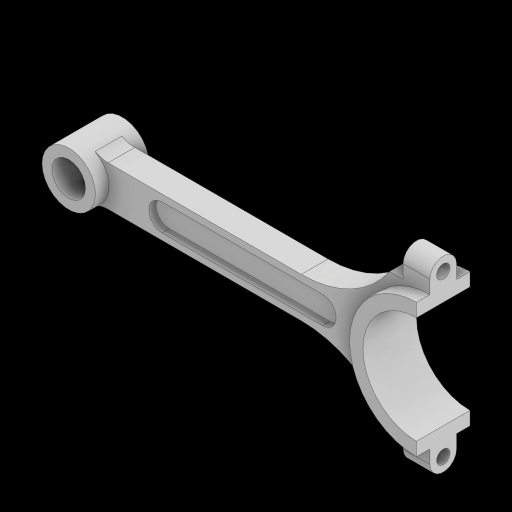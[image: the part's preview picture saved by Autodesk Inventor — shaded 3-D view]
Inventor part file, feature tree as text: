
AUTODESK INVENTOR PART (.ipt)
format: ipt  version: 2024 (Build 280153000, 153)  size: 208,384 bytes
history: native  units: in
note: dims shown in document units (in); Inventor stores cm internally (conversion verified against a paired STEP export)
features: sketch x3, extrude x3, fillet x2, mirror x2, hole x1
ambient origin geometry x8: Origin, YZ Plane, XZ Plane, XY Plane, X Axis, Y Axis, Z Axis, Center Point
bodies: Solid1 (feature_tree)
feature tree (11):
  sketch  "Sketch1"  dims[d0=2.0in d1=1.0in]
  extrude  "CENTER WEB"  Depth=1.0in
  extrude  "END RINGS"  Depth=0.625in
  fillet  "Fillet1"  Radius=2.5in
  fillet  "Fillet2"  Radius=0.75in
  hole  "Hole1"  [1 undecoded]
  mirror  "Mirror1"
  extrude  "RIGHT POCKET"  Depth=0.5in
  mirror  "Mirror2"
  sketch  "Sketch2"  dims[d2=6.5in d3=0.625in d4=2.5in d5=0.75in]
  sketch  "Sketch3"  dims[d6=0.375in d7=1.75in d8=0.5in d10=0.75in d11=1.25in d12=4.0in d14=0.5in d15=0.0in d16=1.0in d17=0.0in d18=0.5in d19=0.25in d20=0.25in d21=0.75in d22=0.375in d23=0.25in d24=0.5635in d25=1.0in d26=0.8108in d27=0.25in d28=3.0in d29=2.0in d30=0.25in d31=0.125in d32=0.0in]
note: 1 required parameter value undecoded (feature->parameter linkage not recoverable at this tier; creation-order binding heuristic only, values carry confidence <= 0.55)
